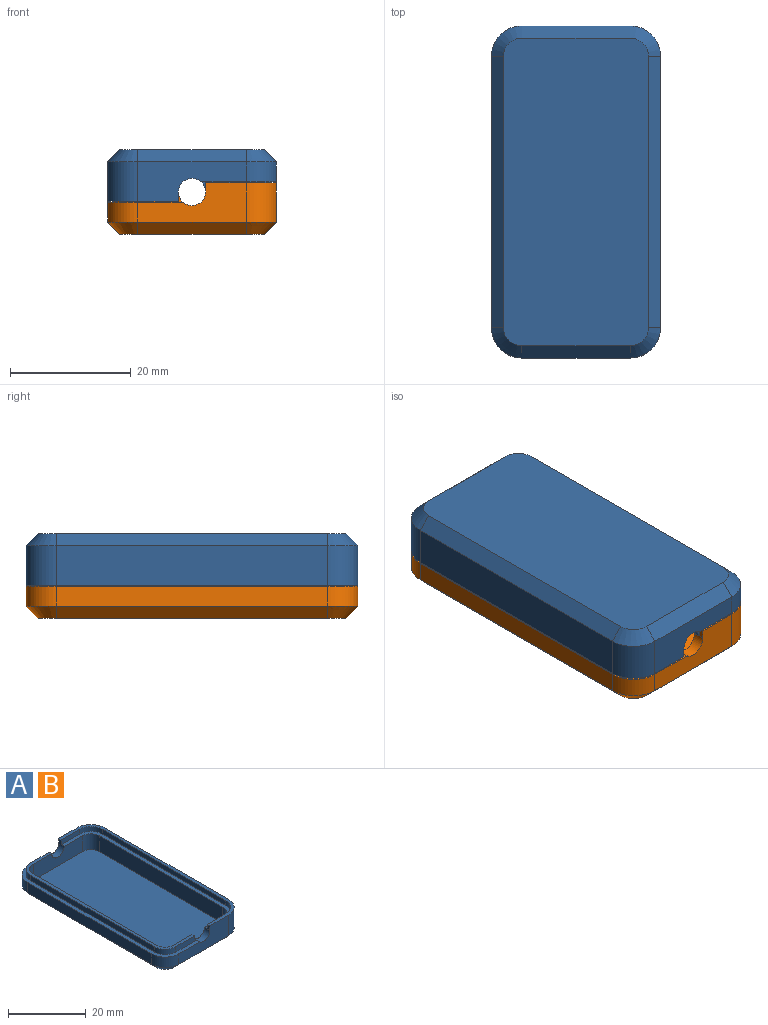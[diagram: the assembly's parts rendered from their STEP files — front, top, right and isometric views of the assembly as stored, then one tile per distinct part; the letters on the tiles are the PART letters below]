
ASSEMBLY  parts=2 mates=1
PART A: 44 faces, bbox 28x55x8.5 mm
  f0: plane 18x6.5mm, normal (0,-1,0), area 80.3mm2, adj f2,f10,f11,f27,f30,f35,f40
  f1: plane 18x6.5mm, normal (0,1,0), area 80.3mm2, adj f8,f9,f21,f27,f31,f35,f39
  f2: cylinder r=2.25mm len=4.5mm, axis (0,-1,0), area 12mm2, adj f0,f3,f5,f15,f23,f27,f30
  f3: plane 53.2x10.85mm, normal (0,0,1), area 76.6mm2, adj f2,f12,f13,f15,f17,f20,f21,f28
  f4: plane 45x3.3mm, normal (-1,0,0), area 148.5mm2, adj f9,f10,f27,f43
  f5: plane 52.8x10.65mm, normal (0,0,1), area 62.4mm2, adj f2,f13,f14,f15,f18,f19,f21,f22
  f6: plane 45x6.5mm, normal (1,0,0), area 292.5mm2, adj f8,f11,f35,f36
  f7: plane 51x24mm, normal (0,0,-1), area 1216.3mm2, adj f36,f37,f38,f39,f40,f41,f42,f43
  f8: cylinder r=5mm len=6.5mm, axis (0,0,1), area 51.1mm2, adj f1,f6,f35,f37
  f9: cylinder r=5mm len=5mm, axis (0,0,-1), area 25.9mm2, adj f1,f4,f27,f41
  f10: cylinder r=5mm len=5mm, axis (0,0,1), area 25.9mm2, adj f0,f4,f27,f42
  f11: cylinder r=5mm len=6.5mm, axis (0,0,-1), area 51.1mm2, adj f0,f6,f35,f38
  f12: plane 45x5mm, normal (-1,0,0), area 225mm2, adj f3,f16,f17,f20
  f13: plane 18x5mm, normal (0,-1,0), area 82mm2, adj f3,f5,f16,f17,f18,f21
  f14: plane 45x5mm, normal (1,0,0), area 225mm2, adj f5,f16,f18,f19
  f15: plane 18x5mm, normal (0,1,0), area 82mm2, adj f2,f3,f5,f16,f19,f20
  f16: plane 51x24mm, normal (0,0,1), area 1216.3mm2, adj f12,f13,f14,f15,f17,f18,f19,f20
  f17: cylinder r=3mm len=5mm, axis (0,0,1), area 23.6mm2, adj f3,f12,f13,f16
  f18: cylinder r=3mm len=5mm, axis (0,0,-1), area 23.6mm2, adj f5,f13,f14,f16
  f19: cylinder r=3mm len=5mm, axis (0,0,1), area 23.6mm2, adj f5,f14,f15,f16
  f20: cylinder r=3mm len=5mm, axis (0,0,-1), area 23.6mm2, adj f3,f12,f15,f16
  f21: cylinder r=2.25mm len=4.5mm, axis (0,-1,0), area 12mm2, adj f1,f3,f5,f13,f22,f27,f31
  f22: plane 7.53x1.7mm, normal (0,1,0), area 11.9mm2, adj f5,f21,f26,f27
  f23: plane 7.53x1.7mm, normal (0,-1,0), area 11.9mm2, adj f2,f5,f24,f27
  f24: cylinder r=3.9mm len=3.9mm, axis (0,0,1), area 10.4mm2, adj f5,f23,f25,f27
  f25: plane 45x1.7mm, normal (-1,0,0), area 76.5mm2, adj f5,f24,f26,f27
  f26: cylinder r=3.9mm len=3.9mm, axis (0,0,1), area 10.4mm2, adj f5,f22,f25,f27
  f27: plane 55x12.53mm, normal (0,0,1), area 81.4mm2, adj f0,f1,f2,f4,f9,f10,f21,f22
  f28: cylinder r=4.1mm len=4.1mm, axis (0,0,-1), area 9.7mm2, adj f3,f29,f34,f35
  f29: plane 6.75x1.5mm, normal (0,1,0), area 10.1mm2, adj f3,f28,f30,f35
  f30: plane 1.5x0.9mm, normal (-1,0,0), area 1.3mm2, adj f0,f2,f29,f35
  f31: plane 1.5x0.9mm, normal (-1,0,0), area 1.4mm2, adj f1,f21,f32,f35
  f32: plane 6.75x1.5mm, normal (0,-1,0), area 10.1mm2, adj f3,f31,f33,f35
  f33: cylinder r=4.1mm len=4.1mm, axis (0,0,-1), area 9.7mm2, adj f3,f32,f34,f35
  f34: plane 45x1.5mm, normal (-1,0,0), area 67.5mm2, adj f3,f28,f33,f35
  f35: plane 55x11.75mm, normal (0,0,1), area 65.5mm2, adj f0,f1,f6,f8,f11,f28,f29,f30
  f36: plane 45x2mm, normal (0.71,0,-0.71), area 127.3mm2, adj f6,f7,f37,f38
  f37: cone r=3mm half-angle=45deg, axis (0,0,1), area 17.8mm2, adj f7,f8,f36,f39
  f38: cone r=3mm half-angle=45deg, axis (0,0,1), area 17.8mm2, adj f7,f11,f36,f40
  f39: plane 18x2mm, normal (0,0.71,-0.71), area 50.9mm2, adj f1,f7,f37,f41
  f40: plane 18x2mm, normal (0,-0.71,-0.71), area 50.9mm2, adj f0,f7,f38,f42
  f41: cone r=3mm half-angle=45deg, axis (0,0,1), area 17.8mm2, adj f7,f9,f39,f43
  f42: cone r=3mm half-angle=45deg, axis (0,0,1), area 17.8mm2, adj f7,f10,f40,f43
  f43: plane 45x2mm, normal (-0.71,0,-0.71), area 127.3mm2, adj f4,f7,f41,f42
PART B: same geometry as A
PLACE A rot(axis=(0,1,0),180deg) t=(-18.37,-7.46,18.73)mm
PLACE B t=(-18.37,-7.46,4.73)mm
MATE fastened A.f10 <-> B.f11  axis (0,0,-1) through (-9.37,-29.96,11.73)mm
